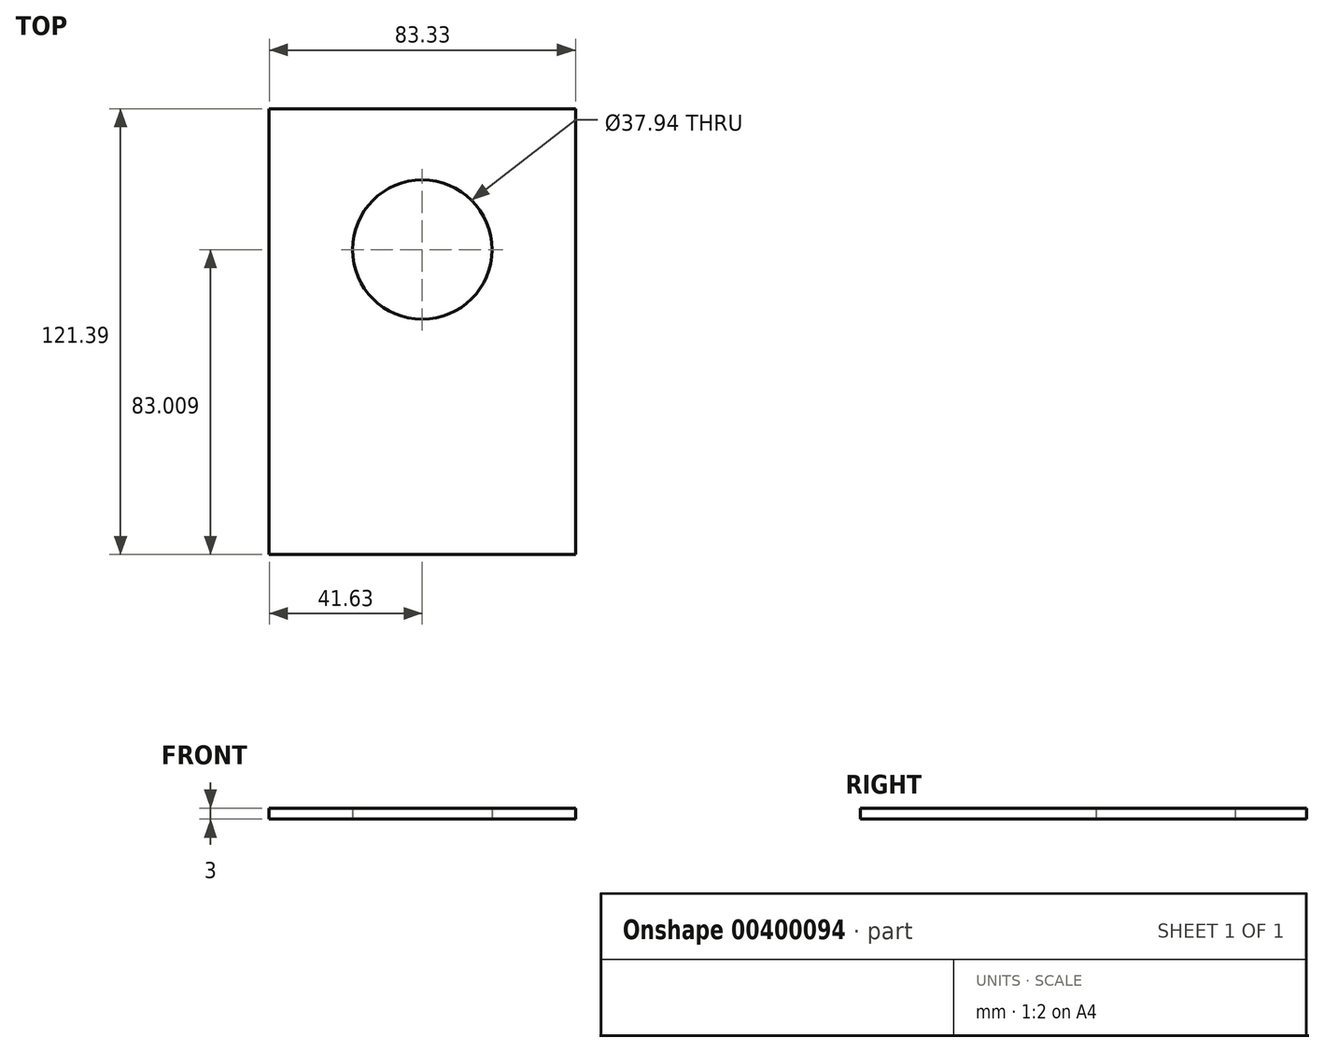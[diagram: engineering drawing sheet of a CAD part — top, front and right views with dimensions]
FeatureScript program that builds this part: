
annotation { "Feature Type Name" : "Feature", "Feature Type Description" : "" }
export const myFeature = defineFeature(function(context is Context, id is Id, definition is map)
    precondition{}
    {
        {
            var Q0;
            Q0=qCreatedBy(makeId("Top.planeOp"),FACE);
            var sketch = newSketch(context, id + "F0", { "sketchPlane" : qUnion([Q0])});
            skLineSegment(sketch, "E0.bottom", {"start": v(41.7, 60.14) * mm, "end": v(-41.63, 60.14) * mm});
            skLineSegment(sketch, "E0.top", {"start": v(41.7, -61.25) * mm, "end": v(-41.63, -61.25) * mm});
            skLineSegment(sketch, "E0.left", {"start": v(41.7, 60.14) * mm, "end": v(41.7, -61.25) * mm});
            skLineSegment(sketch, "E0.right", {"start": v(-41.63, 60.14) * mm, "end": v(-41.63, -61.25) * mm});
            skPoint(sketch, "E0.middle", {"position": v(0.03, -0.55) * mm});
            skCircle(sketch, "E1", {"center": v(0, 21.76) * mm, "radius": 18.97 * mm});
            skSolve(sketch);
        }
        {
            var Q0;
            Q0=makeQuery(id+"F0.imprint","IMPRINT",FACE,{"disambiguationData":[TD([[makeQuery(id+"F0.imprint","IMPRINT",EDGE,{"derivedFrom":sQuery(id+"F0.wireOp",EDGE,"E0.bottom")}),1.0]])]});
            extrude(context, id + "F1", {"entities" : qUnion([Q0]), "depth" : 3 * mm});
        }
    });
